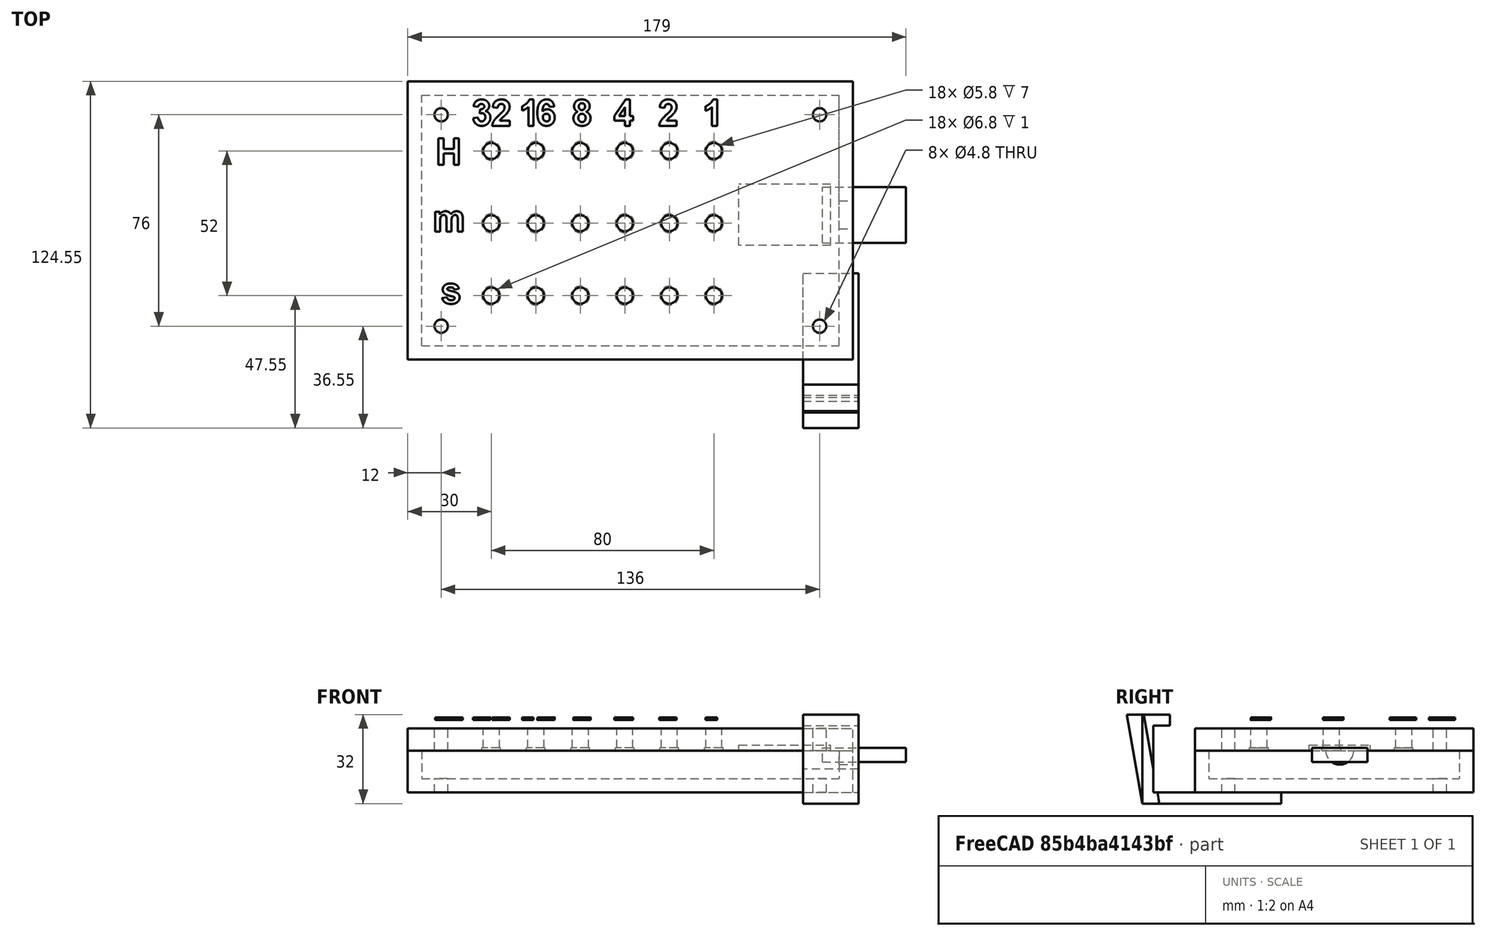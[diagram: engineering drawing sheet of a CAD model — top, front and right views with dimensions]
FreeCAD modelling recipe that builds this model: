
FCSTD DOCUMENT  (FreeCAD 0.18R16117 (Git))
Label: dioda1
License: All rights reserved
LicenseURL: http://en.wikipedia.org/wiki/All_rights_reserved
objects: Part::Cylinder×39, Part::MultiFuse×29, Part::Box×15, Part::Part2DObjectPython×11, Part::Extrusion×11, Part::Cut×6, App::DocumentObjectGroup×1
note: 111 computed .brp shape members not serialized (recipe doc carries the construction recipe); baked Part::Feature solids carry a one-line shape summary decoded from their .brp

FEATURE [Part::Cylinder] Cylinder
  Angle = 360
  AttacherType = Attacher::AttachEngine3D
  Height = 10
  Placement = pos=(5,5,0) rot=(0,0,1;0rad)
  Radius = 2.9
FEATURE [Part::Cylinder] Cylinder001
  Angle = 360
  AttacherType = Attacher::AttachEngine3D
  Height = 1
  Placement = pos=(5,5,0) rot=(0,0,1;0rad)
  Radius = 3.4
FEATURE [Part::Box] Box001  label="FrontPanel"
  AttacherType = Attacher::AttachEngine3D
  Height = 8
  Length = 160
  Width = 100
FEATURE [Part::MultiFuse] Fusion
  Placement = pos=(25,70,0) rot=(0,0,1;0rad)
  Shapes = -> [Cylinder,Cylinder001]
FEATURE [Part::Cylinder] Cylinder002
  Angle = 360
  AttacherType = Attacher::AttachEngine3D
  Height = 1
  Placement = pos=(5,5,0) rot=(0,0,1;0rad)
  Radius = 3.4
FEATURE [Part::Cylinder] Cylinder003
  Angle = 360
  AttacherType = Attacher::AttachEngine3D
  Height = 10
  Placement = pos=(5,5,0) rot=(0,0,1;0rad)
  Radius = 2.9
FEATURE [Part::MultiFuse] Fusion001
  Placement = pos=(41,70,0) rot=(0,0,1;0rad)
  Shapes = -> [Cylinder003,Cylinder002]
FEATURE [Part::Cylinder] Cylinder004
  Angle = 360
  AttacherType = Attacher::AttachEngine3D
  Height = 1
  Placement = pos=(5,5,0) rot=(0,0,1;0rad)
  Radius = 3.4
FEATURE [Part::Cylinder] Cylinder005
  Angle = 360
  AttacherType = Attacher::AttachEngine3D
  Height = 10
  Placement = pos=(5,5,0) rot=(0,0,1;0rad)
  Radius = 2.9
FEATURE [Part::MultiFuse] Fusion002
  Placement = pos=(57,70,0) rot=(0,0,1;0rad)
  Shapes = -> [Cylinder005,Cylinder004]
FEATURE [Part::Cylinder] Cylinder006
  Angle = 360
  AttacherType = Attacher::AttachEngine3D
  Height = 1
  Placement = pos=(5,5,0) rot=(0,0,1;0rad)
  Radius = 3.4
FEATURE [Part::Cylinder] Cylinder007
  Angle = 360
  AttacherType = Attacher::AttachEngine3D
  Height = 10
  Placement = pos=(5,5,0) rot=(0,0,1;0rad)
  Radius = 2.9
FEATURE [Part::MultiFuse] Fusion003
  Placement = pos=(73,70,0) rot=(0,0,1;0rad)
  Shapes = -> [Cylinder007,Cylinder006]
FEATURE [Part::Cylinder] Cylinder008
  Angle = 360
  AttacherType = Attacher::AttachEngine3D
  Height = 1
  Placement = pos=(5,5,0) rot=(0,0,1;0rad)
  Radius = 3.4
FEATURE [Part::Cylinder] Cylinder009
  Angle = 360
  AttacherType = Attacher::AttachEngine3D
  Height = 10
  Placement = pos=(5,5,0) rot=(0,0,1;0rad)
  Radius = 2.9
FEATURE [Part::MultiFuse] Fusion004
  Placement = pos=(89,70,0) rot=(0,0,1;0rad)
  Shapes = -> [Cylinder009,Cylinder008]
FEATURE [Part::MultiFuse] Fusion005
  Placement = pos=(105,70,0) rot=(0,0,1;0rad)
  Shapes = -> [Cylinder009,Cylinder008]
FEATURE [Part::MultiFuse] Fusion006
  Shapes = -> [Fusion,Fusion001,Fusion002,Fusion003,Fusion004,Fusion005]
FEATURE [Part::Cylinder] Cylinder010
  Angle = 360
  AttacherType = Attacher::AttachEngine3D
  Height = 1
  Placement = pos=(5,5,0) rot=(0,0,1;0rad)
  Radius = 3.4
FEATURE [Part::Cylinder] Cylinder011
  Angle = 360
  AttacherType = Attacher::AttachEngine3D
  Height = 1
  Placement = pos=(5,5,0) rot=(0,0,1;0rad)
  Radius = 3.4
FEATURE [Part::Cylinder] Cylinder012
  Angle = 360
  AttacherType = Attacher::AttachEngine3D
  Height = 10
  Placement = pos=(5,5,0) rot=(0,0,1;0rad)
  Radius = 2.9
FEATURE [Part::Cylinder] Cylinder013
  Angle = 360
  AttacherType = Attacher::AttachEngine3D
  Height = 10
  Placement = pos=(5,5,0) rot=(0,0,1;0rad)
  Radius = 2.9
FEATURE [Part::Cylinder] Cylinder014
  Angle = 360
  AttacherType = Attacher::AttachEngine3D
  Height = 1
  Placement = pos=(5,5,0) rot=(0,0,1;0rad)
  Radius = 3.4
FEATURE [Part::MultiFuse] Fusion007
  Placement = pos=(41,70,0) rot=(0,0,1;0rad)
  Shapes = -> [Cylinder013,Cylinder011]
FEATURE [Part::MultiFuse] Fusion009
  Placement = pos=(25,70,0) rot=(0,0,1;0rad)
  Shapes = -> [Cylinder012,Cylinder010]
FEATURE [Part::Cylinder] Cylinder015
  Angle = 360
  AttacherType = Attacher::AttachEngine3D
  Height = 10
  Placement = pos=(5,5,0) rot=(0,0,1;0rad)
  Radius = 2.9
FEATURE [Part::Cylinder] Cylinder016
  Angle = 360
  AttacherType = Attacher::AttachEngine3D
  Height = 10
  Placement = pos=(5,5,0) rot=(0,0,1;0rad)
  Radius = 2.9
FEATURE [Part::MultiFuse] Fusion010
  Placement = pos=(57,70,0) rot=(0,0,1;0rad)
  Shapes = -> [Cylinder016,Cylinder014]
FEATURE [Part::Cylinder] Cylinder017
  Angle = 360
  AttacherType = Attacher::AttachEngine3D
  Height = 1
  Placement = pos=(5,5,0) rot=(0,0,1;0rad)
  Radius = 3.4
FEATURE [Part::Cylinder] Cylinder018
  Angle = 360
  AttacherType = Attacher::AttachEngine3D
  Height = 1
  Placement = pos=(5,5,0) rot=(0,0,1;0rad)
  Radius = 3.4
FEATURE [Part::MultiFuse] Fusion012
  Placement = pos=(73,70,0) rot=(0,0,1;0rad)
  Shapes = -> [Cylinder015,Cylinder018]
FEATURE [Part::Cylinder] Cylinder019
  Angle = 360
  AttacherType = Attacher::AttachEngine3D
  Height = 10
  Placement = pos=(5,5,0) rot=(0,0,1;0rad)
  Radius = 2.9
FEATURE [Part::MultiFuse] Fusion008
  Placement = pos=(105,70,0) rot=(0,0,1;0rad)
  Shapes = -> [Cylinder019,Cylinder017]
FEATURE [Part::MultiFuse] Fusion011
  Placement = pos=(89,70,0) rot=(0,0,1;0rad)
  Shapes = -> [Cylinder019,Cylinder017]
FEATURE [Part::MultiFuse] Fusion013
  Placement = pos=(0,-26,0) rot=(0,0,1;0rad)
  Shapes = -> [Fusion009,Fusion007,Fusion010,Fusion012,Fusion011,Fusion008]
FEATURE [Part::Cylinder] Cylinder020
  Angle = 360
  AttacherType = Attacher::AttachEngine3D
  Height = 10
  Placement = pos=(5,5,0) rot=(0,0,1;0rad)
  Radius = 2.9
FEATURE [Part::Cylinder] Cylinder021
  Angle = 360
  AttacherType = Attacher::AttachEngine3D
  Height = 10
  Placement = pos=(5,5,0) rot=(0,0,1;0rad)
  Radius = 2.9
FEATURE [Part::Cylinder] Cylinder022
  Angle = 360
  AttacherType = Attacher::AttachEngine3D
  Height = 10
  Placement = pos=(5,5,0) rot=(0,0,1;0rad)
  Radius = 2.9
FEATURE [Part::Cylinder] Cylinder023
  Angle = 360
  AttacherType = Attacher::AttachEngine3D
  Height = 1
  Placement = pos=(5,5,0) rot=(0,0,1;0rad)
  Radius = 3.4
FEATURE [Part::MultiFuse] Fusion016
  Placement = pos=(25,70,0) rot=(0,0,1;0rad)
  Shapes = -> [Cylinder021,Cylinder023]
FEATURE [Part::Cylinder] Cylinder024
  Angle = 360
  AttacherType = Attacher::AttachEngine3D
  Height = 10
  Placement = pos=(5,5,0) rot=(0,0,1;0rad)
  Radius = 2.9
FEATURE [Part::Cylinder] Cylinder025
  Angle = 360
  AttacherType = Attacher::AttachEngine3D
  Height = 1
  Placement = pos=(5,5,0) rot=(0,0,1;0rad)
  Radius = 3.4
FEATURE [Part::MultiFuse] Fusion020
  Placement = pos=(57,70,0) rot=(0,0,1;0rad)
  Shapes = -> [Cylinder020,Cylinder025]
FEATURE [Part::Cylinder] Cylinder026
  Angle = 360
  AttacherType = Attacher::AttachEngine3D
  Height = 1
  Placement = pos=(5,5,0) rot=(0,0,1;0rad)
  Radius = 3.4
FEATURE [Part::MultiFuse] Fusion018
  Placement = pos=(41,70,0) rot=(0,0,1;0rad)
  Shapes = -> [Cylinder024,Cylinder026]
FEATURE [Part::Cylinder] Cylinder027
  Angle = 360
  AttacherType = Attacher::AttachEngine3D
  Height = 10
  Placement = pos=(5,5,0) rot=(0,0,1;0rad)
  Radius = 2.9
FEATURE [Part::Cylinder] Cylinder028
  Angle = 360
  AttacherType = Attacher::AttachEngine3D
  Height = 1
  Placement = pos=(5,5,0) rot=(0,0,1;0rad)
  Radius = 3.4
FEATURE [Part::MultiFuse] Fusion014
  Placement = pos=(105,70,0) rot=(0,0,1;0rad)
  Shapes = -> [Cylinder027,Cylinder028]
FEATURE [Part::MultiFuse] Fusion015
  Placement = pos=(89,70,0) rot=(0,0,1;0rad)
  Shapes = -> [Cylinder027,Cylinder028]
FEATURE [Part::Cylinder] Cylinder029
  Angle = 360
  AttacherType = Attacher::AttachEngine3D
  Height = 1
  Placement = pos=(5,5,0) rot=(0,0,1;0rad)
  Radius = 3.4
FEATURE [Part::MultiFuse] Fusion019
  Placement = pos=(73,70,0) rot=(0,0,1;0rad)
  Shapes = -> [Cylinder022,Cylinder029]
FEATURE [Part::MultiFuse] Fusion017
  Placement = pos=(0,-52,0) rot=(0,0,1;0rad)
  Shapes = -> [Fusion016,Fusion018,Fusion020,Fusion019,Fusion015,Fusion014]
FEATURE [Part::MultiFuse] Fusion021  label="Diody"
  Shapes = -> [Fusion006,Fusion013,Fusion017]
FEATURE [Part::Box] Box  label="esp8266"
  AttacherType = Attacher::AttachEngine3D
  Height = 5
  Length = 30
  Placement = pos=(149,42,-4) rot=(0,0,1;0rad)
  Width = 20
FEATURE [Part::Box] Box002  label="BackPanel"
  AttacherType = Attacher::AttachEngine3D
  Height = 5
  Length = 160
  Placement = pos=(0,0,-15) rot=(0,0,1;0rad)
  Width = 100
FEATURE [Part::Box] Box003  label="Frame1"
  AttacherType = Attacher::AttachEngine3D
  Height = 10
  Length = 160
  Placement = pos=(0,0,-10) rot=(0,0,1;0rad)
  Width = 5
FEATURE [Part::Box] Box004  label="Frame2"
  AttacherType = Attacher::AttachEngine3D
  Height = 10
  Length = 160
  Placement = pos=(0,95,-10) rot=(0,0,1;0rad)
  Width = 5
FEATURE [Part::Box] Box005  label="Frame3"
  AttacherType = Attacher::AttachEngine3D
  Height = 10
  Length = 5
  Placement = pos=(0,0,-10) rot=(0,0,1;0rad)
  Width = 100
FEATURE [Part::Box] Box006  label="Kostka003"
  AttacherType = Attacher::AttachEngine3D
  Height = 10
  Length = 5
  Placement = pos=(195,0,-10) rot=(0,0,1;0rad)
  Width = 100
FEATURE [Part::Cylinder] Cylinder030
  Angle = 360
  AttacherType = Attacher::AttachEngine3D
  Height = 10
  Placement = pos=(192,52,-3e-15) rot=(0,1,0;1.5708rad)
  Radius = 5
FEATURE [Part::Cut] Cut  label="Frame4"
  Base = -> Box006
  Placement = pos=(-40,0,0) rot=(0,0,1;0rad)
  Tool = -> Cylinder030
FEATURE [Part::Box] Box007  label="esp8267"
  AttacherType = Attacher::AttachEngine3D
  Height = 5
  Length = 33
  Placement = pos=(119,41,-3) rot=(0,0,1;0rad)
  Width = 22
FEATURE [Part::Cut] Cut001  label="FrontPanel001"
  Base = -> Box001
  Tool = -> Fusion021
FEATURE [Part::Cut] Cut002  label="Front002"
  Base = -> Cut001
  Tool = -> Box007
FEATURE [Part::MultiFuse] Fusion022  label="Frame"
  Shapes = -> [Box003,Box004,Box005,Cut]
FEATURE [Part::Cylinder] Cylinder031
  Angle = 360
  AttacherType = Attacher::AttachEngine3D
  Height = 10
  Placement = pos=(148,88,-15) rot=(0,0,1;0rad)
  Radius = 2.4
FEATURE [Part::Cylinder] Cylinder032
  Angle = 360
  AttacherType = Attacher::AttachEngine3D
  Height = 10
  Placement = pos=(148,12,-15) rot=(0,0,1;0rad)
  Radius = 2.4
FEATURE [Part::Cylinder] Cylinder033
  Angle = 360
  AttacherType = Attacher::AttachEngine3D
  Height = 10
  Placement = pos=(12,88,-15) rot=(0,0,1;0rad)
  Radius = 2.4
FEATURE [Part::Cylinder] Cylinder034
  Angle = 360
  AttacherType = Attacher::AttachEngine3D
  Height = 10
  Placement = pos=(12,12,-15) rot=(0,0,1;0rad)
  Radius = 2.4
FEATURE [Part::MultiFuse] Fusion023  label="screws"
  Placement = pos=(0,0,-3) rot=(0,0,1;0rad)
  Shapes = -> [Cylinder031,Cylinder032,Cylinder033,Cylinder034]
FEATURE [Part::Cut] Cut003  label="BackPanel001"
  Base = -> Box002
  Tool = -> Fusion023
FEATURE [Part::Cylinder] Cylinder035
  Angle = 360
  AttacherType = Attacher::AttachEngine3D
  Height = 10
  Placement = pos=(148,88,-15) rot=(0,0,1;0rad)
  Radius = 2.4
FEATURE [Part::Cylinder] Cylinder036
  Angle = 360
  AttacherType = Attacher::AttachEngine3D
  Height = 10
  Placement = pos=(148,12,-15) rot=(0,0,1;0rad)
  Radius = 2.4
FEATURE [Part::Cylinder] Cylinder037
  Angle = 360
  AttacherType = Attacher::AttachEngine3D
  Height = 10
  Placement = pos=(12,88,-15) rot=(0,0,1;0rad)
  Radius = 2.4
FEATURE [Part::Cylinder] Cylinder038
  Angle = 360
  AttacherType = Attacher::AttachEngine3D
  Height = 10
  Placement = pos=(12,12,-15) rot=(0,0,1;0rad)
  Radius = 2.4
FEATURE [Part::MultiFuse] Fusion024  label="screws001"
  Placement = pos=(0,0,14) rot=(0,0,1;0rad)
  Shapes = -> [Cylinder035,Cylinder036,Cylinder037,Cylinder038]
FEATURE [Part::Cut] Cut004  label="Front"
  Base = -> Cut002
  Tool = -> Fusion024
FEATURE [Part::MultiFuse] Fusion025  label="Back"
  Shapes = -> [Fusion022,Cut003]
FEATURE [Part::Part2DObjectPython] ShapeString  # Draft 2D object (typed FeaturePython)
  FontFile = <userpath>/Desktop/ARIALBD.TTF
  Placement = pos=(-149,13,0) rot=(0,0,1;0rad)
  Size = 10
  String = H
  Tracking = 0
FEATURE [Part::Part2DObjectPython] ShapeString001  # Draft 2D object (typed FeaturePython)
  FontFile = <userpath>/Desktop/ARIALBD.TTF
  Placement = pos=(-90,41,0) rot=(0,0,1;0rad)
  Size = 10
  String = m
  Tracking = 0
FEATURE [Part::Part2DObjectPython] ShapeString002  # Draft 2D object (typed FeaturePython)
  FontFile = <userpath>/Desktop/ARIALBD.TTF
  Placement = pos=(-96,15,0) rot=(0,0,1;0rad)
  Size = 10
  String = s
  Tracking = 0
FEATURE [Part::Extrusion] Extrude  label="H"
  Base = -> ShapeString
  Dir = (0,0,1)
  DirMode = 2
  FaceMakerClass = Part::FaceMakerBullseye
  LengthFwd = 1
  LengthRev = 0
  Placement = pos=(159,57,11) rot=(0,0,1;0rad)
  Solid = false
  Symmetric = false
FEATURE [Part::Extrusion] Extrude001  label="m"
  Base = -> ShapeString001
  Dir = (0,0,1)
  DirMode = 2
  FaceMakerClass = Part::FaceMakerBullseye
  LengthFwd = 1
  LengthRev = 0
  Placement = pos=(99,5,11) rot=(0,0,1;0rad)
  Solid = false
  Symmetric = false
FEATURE [Part::Extrusion] Extrude002  label="s"
  Base = -> ShapeString002
  Dir = (0,0,1)
  DirMode = 2
  FaceMakerClass = Part::FaceMakerBullseye
  LengthFwd = 1
  LengthRev = 0
  Placement = pos=(108,5,11) rot=(0,0,1;0rad)
  Solid = false
  Symmetric = false
FEATURE [Part::Part2DObjectPython] ShapeString003  # Draft 2D object (typed FeaturePython)
  FontFile = <userpath>/Desktop/ARIALBD.TTF
  Placement = pos=(-86,60,0) rot=(0,0,1;0rad)
  Size = 10
  String = 3
  Tracking = 0
FEATURE [Part::Part2DObjectPython] ShapeString004  # Draft 2D object (typed FeaturePython)
  FontFile = <userpath>/Desktop/ARIALBD.TTF
  Placement = pos=(-66,65,0) rot=(0,0,1;0rad)
  Size = 10
  String = 2
  Tracking = 0
FEATURE [Part::Part2DObjectPython] ShapeString005  # Draft 2D object (typed FeaturePython)
  FontFile = <userpath>/Desktop/ARIALBD.TTF
  Placement = pos=(-104,79,0) rot=(0,0,1;0rad)
  Size = 10
  String = 1
  Tracking = 0
FEATURE [Part::Part2DObjectPython] ShapeString006  # Draft 2D object (typed FeaturePython)
  FontFile = <userpath>/Desktop/ARIALBD.TTF
  Placement = pos=(-106,73,0) rot=(0,0,1;0rad)
  Size = 10
  String = 6
  Tracking = 0
FEATURE [Part::Part2DObjectPython] ShapeString007  # Draft 2D object (typed FeaturePython)
  FontFile = <userpath>/Desktop/ARIALBD.TTF
  Placement = pos=(-107,77,0) rot=(0,0,1;0rad)
  Size = 10
  String = 8
  Tracking = 0
FEATURE [Part::Part2DObjectPython] ShapeString008  # Draft 2D object (typed FeaturePython)
  FontFile = <userpath>/Desktop/ARIALBD.TTF
  Placement = pos=(-78,83,0) rot=(0,0,1;0rad)
  Size = 10
  String = 4
  Tracking = 0
FEATURE [App::DocumentObjectGroup] Construction
  Group = -> [ShapeString,ShapeString001,ShapeString002,ShapeString003,ShapeString004,ShapeString005,ShapeString006,ShapeString007,ShapeString008]
FEATURE [Part::Extrusion] Extrude003  label="3"
  Base = -> ShapeString003
  Dir = (0,0,1)
  DirMode = 2
  FaceMakerClass = Part::FaceMakerBullseye
  LengthFwd = 1
  LengthRev = 0
  Placement = pos=(109,24,11) rot=(0,0,1;0rad)
  Solid = false
  Symmetric = false
FEATURE [Part::Extrusion] Extrude004  label="2"
  Base = -> ShapeString004
  Dir = (0,0,1)
  DirMode = 2
  FaceMakerClass = Part::FaceMakerBullseye
  LengthFwd = 1
  LengthRev = 0
  Placement = pos=(96,19,11) rot=(0,0,1;0rad)
  Solid = false
  Symmetric = false
FEATURE [Part::Extrusion] Extrude005  label="1"
  Base = -> ShapeString005
  Dir = (0,0,1)
  DirMode = 2
  FaceMakerClass = Part::FaceMakerBullseye
  LengthFwd = 1
  LengthRev = 0
  Placement = pos=(144,5,11) rot=(0,0,1;0rad)
  Solid = false
  Symmetric = false
FEATURE [Part::Extrusion] Extrude006  label="6"
  Base = -> ShapeString006
  Dir = (0,0,1)
  DirMode = 2
  FaceMakerClass = Part::FaceMakerBullseye
  LengthFwd = 1
  LengthRev = 0
  Placement = pos=(152,11,11) rot=(0,0,1;0rad)
  Solid = false
  Symmetric = false
FEATURE [Part::Extrusion] Extrude007  label="8"
  Base = -> ShapeString007
  Dir = (0,0,1)
  DirMode = 2
  FaceMakerClass = Part::FaceMakerBullseye
  LengthFwd = 1
  LengthRev = 0
  Placement = pos=(166,7,11) rot=(0,0,1;0rad)
  Solid = false
  Symmetric = false
FEATURE [Part::Extrusion] Extrude008  label="4"
  Base = -> ShapeString008
  Dir = (0,0,1)
  DirMode = 2
  FaceMakerClass = Part::FaceMakerBullseye
  LengthFwd = 1
  LengthRev = 0
  Placement = pos=(152,1,11) rot=(0,0,1;0rad)
  Solid = false
  Symmetric = false
FEATURE [Part::Part2DObjectPython] ShapeString009  # Draft 2D object (typed FeaturePython)
  FontFile = <userpath>/Desktop/ARIALBD.TTF
  Placement = pos=(-66,65,0) rot=(0,0,1;0rad)
  Size = 10
  String = 2
  Tracking = 0
FEATURE [Part::Extrusion] Extrude009  label="2(1)"
  Base = -> ShapeString009
  Dir = (0,0,1)
  DirMode = 2
  FaceMakerClass = Part::FaceMakerBullseye
  LengthFwd = 1
  LengthRev = 0
  Placement = pos=(156,19,11) rot=(0,0,1;0rad)
  Solid = false
  Symmetric = false
FEATURE [Part::Part2DObjectPython] ShapeString010  # Draft 2D object (typed FeaturePython)
  FontFile = <userpath>/Desktop/ARIALBD.TTF
  Placement = pos=(-104,79,0) rot=(0,0,1;0rad)
  Size = 10
  String = 1
  Tracking = 0
FEATURE [Part::Extrusion] Extrude010  label="1(1)"
  Base = -> ShapeString010
  Dir = (0,0,1)
  DirMode = 2
  FaceMakerClass = Part::FaceMakerBullseye
  LengthFwd = 1
  LengthRev = 0
  Placement = pos=(210,5,11) rot=(0,0,1;0rad)
  Solid = false
  Symmetric = false
FEATURE [Part::MultiFuse] Fusion026  label="Letters"
  Shapes = -> [Extrude007,Extrude008,Extrude,Extrude001,Extrude002,Extrude009,Extrude005,Extrude003,Extrude004,Extrude010,Extrude006]
FEATURE [Part::Box] Box008  label="Kostka"
  AttacherType = Attacher::AttachEngine3D
  Height = 24
  Length = 20
  Placement = pos=(142,-19,-15) rot=(0,0,1;0rad)
  Width = 4
FEATURE [Part::Box] Box009  label="Kostka004"
  AttacherType = Attacher::AttachEngine3D
  Height = 4
  Length = 20
  Placement = pos=(142,-19,-19) rot=(0,0,1;0rad)
  Width = 50
FEATURE [Part::Box] Box010  label="Kostka005"
  AttacherType = Attacher::AttachEngine3D
  Height = 4
  Length = 20
  Placement = pos=(142,-19,9) rot=(0,0,1;0rad)
  Width = 10
FEATURE [Part::MultiFuse] Fusion027  label="Stopka"
  Shapes = -> [Box008,Box009,Box010]
FEATURE [Part::Box] Box011  label="Kostka006"
  AttacherType = Attacher::AttachEngine3D
  Height = 24
  Length = 20
  Placement = pos=(142,-15,-15) rot=(0,0,1;0rad)
  Width = 6
FEATURE [Part::Box] Box012  label="Kostka007"
  AttacherType = Attacher::AttachEngine3D
  Height = 10
  Length = 20
  Placement = pos=(142,-29,13) rot=(0,0,1;0rad)
  Width = 20
FEATURE [Part::Box] Box013  label="Kostka008"
  AttacherType = Attacher::AttachEngine3D
  Height = 10
  Length = 20
  Placement = pos=(142,-29,-29) rot=(0,0,1;0rad)
  Width = 20
FEATURE [Part::Box] Box014  label="Kostka009"
  AttacherType = Attacher::AttachEngine3D
  Height = 40
  Length = 20
  Placement = pos=(142,-18.5702,-20.9125) rot=(-1,0,0;6.10865rad)
  Width = 6
FEATURE [Part::MultiFuse] Fusion028
  Shapes = -> [Box011,Box013,Box012]
FEATURE [Part::Cut] Cut005
  Base = -> Box014
  Tool = -> Fusion028
